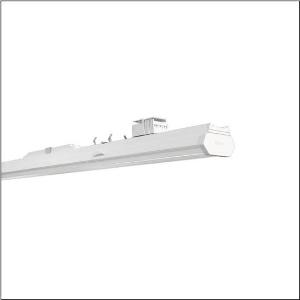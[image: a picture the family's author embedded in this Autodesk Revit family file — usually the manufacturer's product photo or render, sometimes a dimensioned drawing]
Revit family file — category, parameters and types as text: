
# Revit family: licross_r__21_protected_ho_52td12dn4e5m_4ef7
name_source: partatom
category: Lighting Fixtures
units: mm (PartAtom-declared; Revit-internal decimal feet)

## family parameters
Cut with Voids When Loaded = No
Host = Face
Light Source = No
Part Type = Normal
Room Calculation Point = No
Round Connector Dimension = Use Diameter
Shared = No

## types (1)
- --- (1 x LED, 14690 lm, 84.9 W, 4000K)
    Apparent Load = 85 VA
    CIE Flux Codes = 70 91 97 98 100
    Color Rendering = 80
    Color Temperature = 4000K
    Default Elevation = 1800 mm
    Description = Licross® 21 Protected HO, luminaire insert, of sheet steel, galvanised, coil coated, white, length: 1.500mm, width: 90mm, height: 103mm, LED rated luminous flux: 14.690lm, light colour: 840, control gear: DALI 2, with plug, 5-pole, with phase selection, mains connection: 220..240V, AC, 50/60Hz, rated input power: 85W, halogen-free wiring, primary light control with lens, of plastic, primary optical cover: cover, of PMMA, light emission: direct distribution, primary light characteristic: symmetric, protection rating (complete): IP54, insulation class (complete): insulation class I (protective earthing), certification: CE, ENEC, VDE, UKCA, protection symbol: D if used in an environment with non-conductive dust loads with corresponding accessories, impact resistance: IK06, permissible ambient temperature for indoor applications: -25..+35°C, corresponds to IFS (International Featured Standards) requirements for safety and quality in the food industry, reducing of maximum allowable ambient temperature of 5°C with ceiling mounting, LABS conformity tested according to VDMA 24364:2018-05, packaging unit: 1 piece
    Height = 92 mm
    Lamp = 1 x LED
    Lamp Light Flux = 14690 lm
    Lamp Power = 84.9 W
    Lamp count = 1
    Length = 1500 mm
    Luminous efficacy = 173 lm/W
    Manufacturer = Siteco
    ModVariant = No
    Model = 52TD12DN4E5M
    Mounting Place = Ceiling
    Mounting Type = Pendant
    Number of Poles = 1
    OnlyDefault = Yes
    Power Factor = 1
    Product Name = Licross® 21 Protected HO
    Product group = luminaire insert
    ProductGroupID = 901
    Protection Class = Protection class I
    Protection Degree = IP 54
    RLX_Detail_Level = 1
    RLX_Emergency_Light_Flux = 0 lm
    RLX_Emergency_Type = 0
    RLX_Emergency_Type_DB = No
    RlxData = <blob elided: 24433 chars, md5=d7cf2bf1>
    Socket = socket
    Standby Power = 0 W
    System Light Flux = 14690 lm
    System Power = 85 W
    Type Comments = factory setting: luminous flux: 100 % | dim-lin: 254 | 484 mA
    Type Image = l_1256148.jpg
    URL = http://relux.com
    VarID = @adj_060621
    Voltage = 0 V
    Weight = 0.00 kg
    Width = 88 mm

## geometry (parser evidence)
native form markers: Blend x4, Sweep x12
no freeform markers — native parametric forms only
